# Revit family: MC_Window_Template
name_source: partatom
category: Windows
units: mm (PartAtom-declared; Revit-internal decimal feet)

## family parameters
Always vertical = Yes
Cut with Voids When Loaded = No
Host = Wall
OmniClass Number = 23.30.20.00
OmniClass Title = Windows
Room Calculation Point = No
Shared = No

## types (1)
- Test
    Analytic Construction = <None>
    Default Sill Height = 800 mm
    Define Thermal Properties by = Schematic Type
    Det_03Fine_Distance btw Frame & Shutter = Yes
    Distance_H_of WIN_from Ext Wall = 0 mm  [stored 0 ft]
    Distance_btw Frame & Shutter = 4 mm  [stored 0.0131234 ft]
    Falsotelaio = Yes
    Falsotelaio_Thickness = 40 mm  [stored 0.131234 ft]
    Falsotelaio_Void_Dist H = 0 mm  [stored 0 ft]
    Frame_Bottom = No
    Frame_BottomElem_Thickness = 50 mm  [stored 0.164042 ft]
    Frame_Depth = 80 mm  [stored 0.262467 ft]
    Frame_Detail_03Fine_Part_A_Depth = 60 mm  [stored 0.19685 ft]
    Frame_Detail_03Fine_Part_A_Thickness = 80 mm  [stored 0.262467 ft]
    Frame_Thickness = 100 mm  [stored 0.328084 ft]
    Height = 2000 mm  [stored 6.56168 ft]
    Height_Net = 1750 mm  [stored 5.74147 ft]
    Shutter_Aggetto_EXT = 0 mm  [stored 0 ft]
    Shutter_Aggetto_INT = 12 mm  [stored 0.0393701 ft]
    Shutter_Detail_03Fine_Part_A_Depth = 20 mm  [stored 0.0656168 ft]
    Shutter_Detail_03Fine_Part_A_Thickness = 20 mm  [stored 0.0656168 ft]
    Shutter_Profile_Thickness = 50 mm  [stored 0.164042 ft]
    Sill_Aggetto_RL = 0 mm  [stored 0 ft]
    Sill_Depth_Ext = 250 mm  [stored 0.82021 ft]
    Sill_Depth_Int = 150 mm
    Sill_Height = 50 mm  [stored 0.164042 ft]
    Sill_Type = Sill_Ext_Int
    Wall Closure = By host
    Width = 1800 mm  [stored 5.90551 ft]
    Width_Net = 1600 mm  [stored 5.24934 ft]

note: [stored X ft] marks values corroborated as IEEE doubles in the binary element streams (Revit-internal decimal feet)

## geometry (parser evidence)
native form markers: Sweep x13
no freeform markers — native parametric forms only
